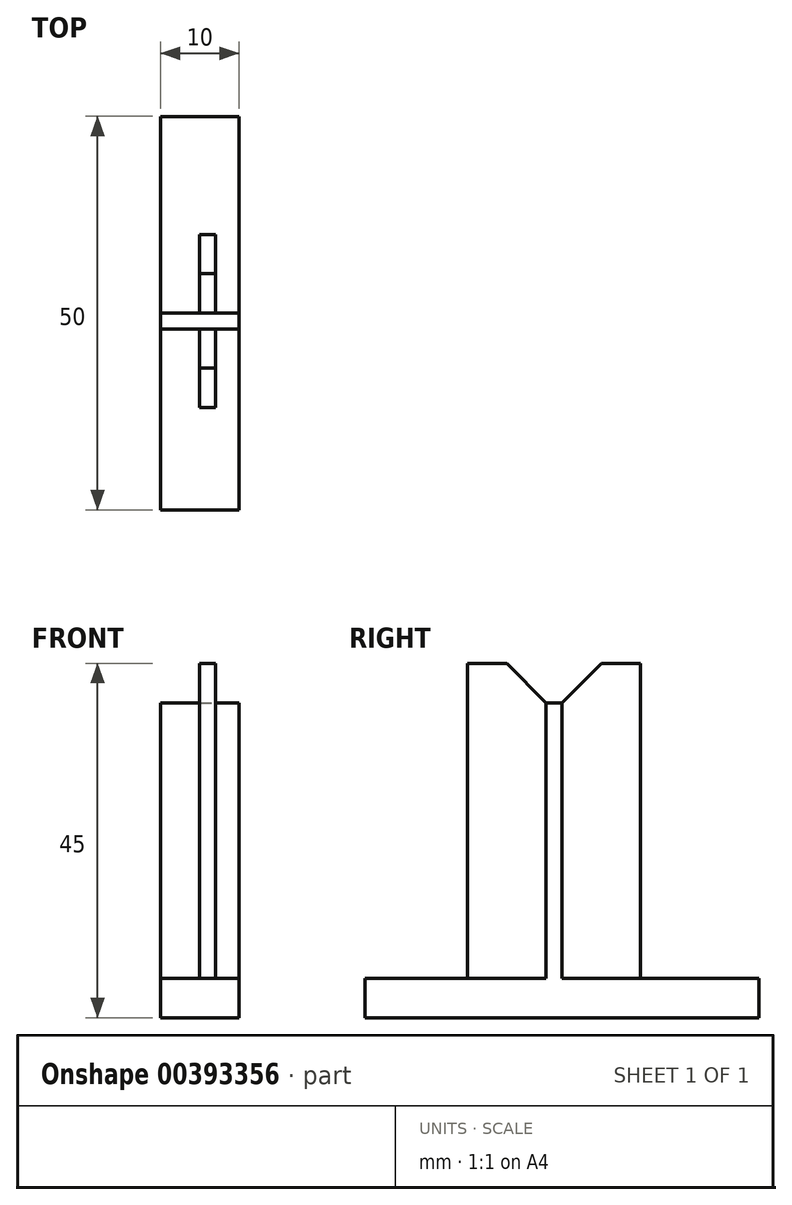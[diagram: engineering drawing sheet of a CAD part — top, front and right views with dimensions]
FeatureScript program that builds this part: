
annotation { "Feature Type Name" : "Feature", "Feature Type Description" : "" }
export const myFeature = defineFeature(function(context is Context, id is Id, definition is map)
    precondition{}
    {
        {
            var Q0;
            Q0=qCreatedBy(makeId("Top.planeOp"),FACE);
            var sketch = newSketch(context, id + "F0", { "sketchPlane" : qUnion([Q0])});
            skLineSegment(sketch, "E0.bottom", {"start": v(-46.24, 34.3) * mm, "end": v(-36.24, 34.3) * mm});
            skLineSegment(sketch, "E0.top", {"start": v(-46.24, -15.7) * mm, "end": v(-36.24, -15.7) * mm});
            skLineSegment(sketch, "E0.left", {"start": v(-46.24, 34.3) * mm, "end": v(-46.24, -15.7) * mm});
            skLineSegment(sketch, "E0.right", {"start": v(-36.24, 34.3) * mm, "end": v(-36.24, -15.7) * mm});
            skSolve(sketch);
        }
        {
            var Q0;
            Q0=makeQuery(id+"F0.imprint","IMPRINT",FACE,{"disambiguationData":[TD([[makeQuery(id+"F0.imprint","IMPRINT",EDGE,{"derivedFrom":sQuery(id+"F0.wireOp",EDGE,"E0.bottom")}),-1.0]])]});
            extrude(context, id + "F1", {"entities" : qUnion([Q0]), "depth" : 5 * mm});
        }
        {
            var Q0;
            Q0=makeQuery(id+"F1.opExtrude","CAP_FACE",FACE,{"disambiguationData":[OSD([sQuery(id+"F0.wireOp",EDGE,"E0.bottom"),sQuery(id+"F0.wireOp",EDGE,"E0.top"),sQuery(id+"F0.wireOp",EDGE,"E0.left"),sQuery(id+"F0.wireOp",EDGE,"E0.right")])],"isStart":false});
            var sketch = newSketch(context, id + "F2", { "sketchPlane" : qUnion([Q0])});
            skLineSegment(sketch, "E1.bottom", {"start": v(-46.24, 9.3) * mm, "end": v(-36.24, 9.3) * mm});
            skLineSegment(sketch, "E1.top", {"start": v(-46.24, 7.3) * mm, "end": v(-36.24, 7.3) * mm});
            skLineSegment(sketch, "E1.left", {"start": v(-46.24, 9.3) * mm, "end": v(-46.24, 7.3) * mm});
            skLineSegment(sketch, "E1.right", {"start": v(-36.24, 9.3) * mm, "end": v(-36.24, 7.3) * mm});
            skSolve(sketch);
        }
        {
            var Q0;
            Q0=makeQuery(id+"F2.imprint","IMPRINT",FACE,{"disambiguationData":[TD([[makeQuery(id+"F2.imprint","IMPRINT",EDGE,{"derivedFrom":sQuery(id+"F2.wireOp",EDGE,"E1.bottom")}),-1.0]])]});
            extrude(context, id + "F3", {"entities" : qUnion([Q0]), "operationType" : NewBodyOperationType.ADD, "depth" : 35 * mm});
        }
        {
            var Q0;
            {var subQ0=sQuery(id+"F0.wireOp",EDGE,"E0.left");var subQ1=sQuery(id+"F0.wireOp",EDGE,"E0.right");var subQ2=sQuery(id+"F0.wireOp",EDGE,"E0.top");Q0=makeQuery(id+"F3.boolean.opBoolean","SPLIT",FACE,{"disambiguationData":[TD([makeQuery(id+"F1.opExtrude","SWEPT_FACE",FACE,{"disambiguationData":[OSD([subQ2])]})])],"derivedFrom":makeQuery(id+"F1.opExtrude","CAP_FACE",FACE,{"disambiguationData":[OSD([sQuery(id+"F0.wireOp",EDGE,"E0.bottom"),subQ2,subQ0,subQ1])],"isStart":false})});}
            var sketch = newSketch(context, id + "F4", { "sketchPlane" : qUnion([Q0])});
            skLineSegment(sketch, "E2.bottom", {"start": v(-41.24, 7.3) * mm, "end": v(-39.24, 7.3) * mm});
            skLineSegment(sketch, "E2.top", {"start": v(-41.24, -2.7) * mm, "end": v(-39.24, -2.7) * mm});
            skLineSegment(sketch, "E2.left", {"start": v(-41.24, 7.3) * mm, "end": v(-41.24, -2.7) * mm});
            skLineSegment(sketch, "E2.right", {"start": v(-39.24, 7.3) * mm, "end": v(-39.24, -2.7) * mm});
            skSolve(sketch);
        }
        {
            var Q0;
            Q0=makeQuery(id+"F4.imprint","IMPRINT",FACE,{"disambiguationData":[TD([[makeQuery(id+"F4.imprint","IMPRINT",EDGE,{"derivedFrom":sQuery(id+"F4.wireOp",EDGE,"E2.bottom")}),-1.0]])]});
            extrude(context, id + "F5", {"entities" : qUnion([Q0]), "depth" : 40 * mm});
        }
        {
            var Q0;
            {var subQ0=sQuery(id+"F0.wireOp",EDGE,"E0.left");var subQ1=sQuery(id+"F0.wireOp",EDGE,"E0.right");var subQ2=sQuery(id+"F0.wireOp",EDGE,"E0.bottom");Q0=makeQuery(id+"F3.boolean.opBoolean","SPLIT",FACE,{"disambiguationData":[TD([makeQuery(id+"F1.opExtrude","SWEPT_FACE",FACE,{"disambiguationData":[OSD([subQ2])]})])],"derivedFrom":makeQuery(id+"F1.opExtrude","CAP_FACE",FACE,{"disambiguationData":[OSD([subQ2,sQuery(id+"F0.wireOp",EDGE,"E0.top"),subQ0,subQ1])],"isStart":false})});}
            var sketch = newSketch(context, id + "F6", { "sketchPlane" : qUnion([Q0])});
            skLineSegment(sketch, "E3.bottom", {"start": v(-41.24, 9.3) * mm, "end": v(-39.24, 9.3) * mm});
            skLineSegment(sketch, "E3.top", {"start": v(-41.24, 19.3) * mm, "end": v(-39.24, 19.3) * mm});
            skLineSegment(sketch, "E3.left", {"start": v(-41.24, 9.3) * mm, "end": v(-41.24, 19.3) * mm});
            skLineSegment(sketch, "E3.right", {"start": v(-39.24, 9.3) * mm, "end": v(-39.24, 19.3) * mm});
            skSolve(sketch);
        }
        {
            var Q0;
            Q0=makeQuery(id+"F6.imprint","IMPRINT",FACE,{"disambiguationData":[TD([[makeQuery(id+"F6.imprint","IMPRINT",EDGE,{"derivedFrom":sQuery(id+"F6.wireOp",EDGE,"E3.bottom")}),1.0]])]});
            extrude(context, id + "F7", {"entities" : qUnion([Q0]), "operationType" : NewBodyOperationType.ADD, "depth" : 40 * mm});
        }
        {
            var Q0;
            Q0=makeQuery(id+"F5.opExtrude","CAP_EDGE",EDGE,{"disambiguationData":[OSD([sQuery(id+"F4.wireOp",EDGE,"E2.bottom")])],"isStart":false});
            chamfer(context, id + "F8", {"entities" : qUnion([Q0]), "width" : 5 * mm, "tangentPropagation" : true});
        }
        {
            var Q0;
            Q0=makeQuery(id+"F7.opExtrude","CAP_EDGE",EDGE,{"disambiguationData":[OSD([sQuery(id+"F6.wireOp",EDGE,"E3.bottom")])],"isStart":false});
            chamfer(context, id + "F9", {"entities" : qUnion([Q0]), "width" : 5 * mm, "tangentPropagation" : true});
        }
    });
